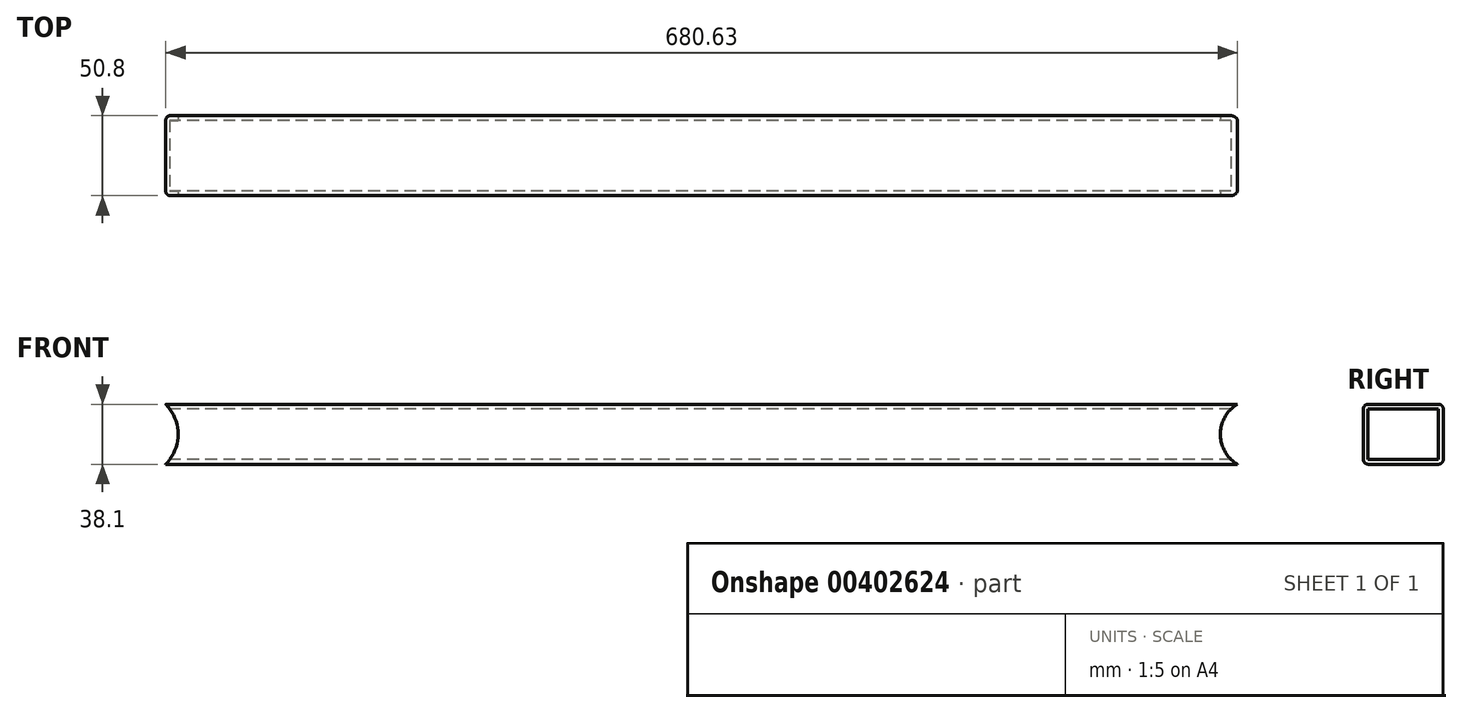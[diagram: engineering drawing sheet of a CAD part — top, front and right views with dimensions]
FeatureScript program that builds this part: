
annotation { "Feature Type Name" : "Feature", "Feature Type Description" : "" }
export const myFeature = defineFeature(function(context is Context, id is Id, definition is map)
    precondition{}
    {
        {
            var Q0;
            Q0=qCreatedBy(makeId("Right.planeOp"),FACE);
            var sketch = newSketch(context, id + "F0", { "sketchPlane" : qUnion([Q0])});
            skLineSegment(sketch, "E0.bottom", {"start": v(-22.35, 19.05) * mm, "end": v(22.35, 19.05) * mm});
            skLineSegment(sketch, "E0.top", {"start": v(-22.35, -19.05) * mm, "end": v(22.35, -19.05) * mm});
            skLineSegment(sketch, "E0.left", {"start": v(-25.4, 16) * mm, "end": v(-25.4, -16) * mm});
            skLineSegment(sketch, "E0.right", {"start": v(25.4, 16) * mm, "end": v(25.4, -16) * mm});
            skPoint(sketch, "E0.middle", {"position": v(0, 0) * mm});
            skPoint(sketch, "E1.visualSharp", {"position": v(-25.4, 19.05) * mm});
            skArc(sketch, "E1.filletArc", {"start": v(-22.35, 19.05) * mm, "mid": v(-24.5, 18.16) * mm, "end": v(-25.4, 16) * mm});
            skPoint(sketch, "E2.visualSharp", {"position": v(25.4, 19.05) * mm});
            skArc(sketch, "E2.filletArc", {"start": v(25.4, 16) * mm, "mid": v(24.5, 18.16) * mm, "end": v(22.35, 19.05) * mm});
            skPoint(sketch, "E3.visualSharp", {"position": v(25.4, -19.05) * mm});
            skArc(sketch, "E3.filletArc", {"start": v(22.35, -19.05) * mm, "mid": v(24.5, -18.16) * mm, "end": v(25.4, -16) * mm});
            skPoint(sketch, "E4.visualSharp", {"position": v(-25.4, -19.05) * mm});
            skArc(sketch, "E4.filletArc", {"start": v(-25.4, -16) * mm, "mid": v(-24.5, -18.16) * mm, "end": v(-22.35, -19.05) * mm});
            skLineSegment(sketch, "E5.bottom", {"start": v(-22.35, 16) * mm, "end": v(22.35, 16) * mm});
            skLineSegment(sketch, "E5.top", {"start": v(-22.35, -16) * mm, "end": v(22.35, -16) * mm});
            skLineSegment(sketch, "E5.left", {"start": v(-22.35, 16) * mm, "end": v(-22.35, -16) * mm});
            skLineSegment(sketch, "E5.right", {"start": v(22.35, 16) * mm, "end": v(22.35, -16) * mm});
            skSolve(sketch);
        }
        {
            var Q0;
            Q0 = qSketchRegion(id + "F0", true);
            extrude(context, id + "F1", {"entities" : qUnion([Q0]), "depth" : 711.2 * mm, "symmetric" : true});
        }
        {
            var Q0;
            Q0=qCreatedBy(makeId("Front.planeOp"),FACE);
            var sketch = newSketch(context, id + "F2", { "sketchPlane" : qUnion([Q0])});
            skLineSegment(sketch, "E6", {"start": v(0, 0) * mm, "end": v(0, 164.65) * mm, "construction": true});
            skCircle(sketch, "E7", {"center": v(-355.6, 0) * mm, "radius": 26.99 * mm});
            skCircle(sketch, "E8.MirrorC", {"center": v(355.6, 0) * mm, "radius": 22.23 * mm});
            skLineSegment(sketch, "E9", {"start": v(-355.6, 0) * mm, "end": v(355.6, 0) * mm, "construction": true});
            skSolve(sketch);
        }
        {
            var Q0;
            Q0 = qSketchRegion(id + "F2", true);
            extrude(context, id + "F3", {"entities" : qUnion([Q0]), "operationType" : NewBodyOperationType.REMOVE, "endBound" : BoundingType.THROUGH_ALL, "oppositeDirection" : true, "depth" : 25.4 * mm, "hasSecondDirection" : true, "secondDirectionBound" : BoundingType.THROUGH_ALL, "secondDirectionOppositeDirection" : false, "secondDirectionDepth" : 25.4 * mm});
        }
    });
